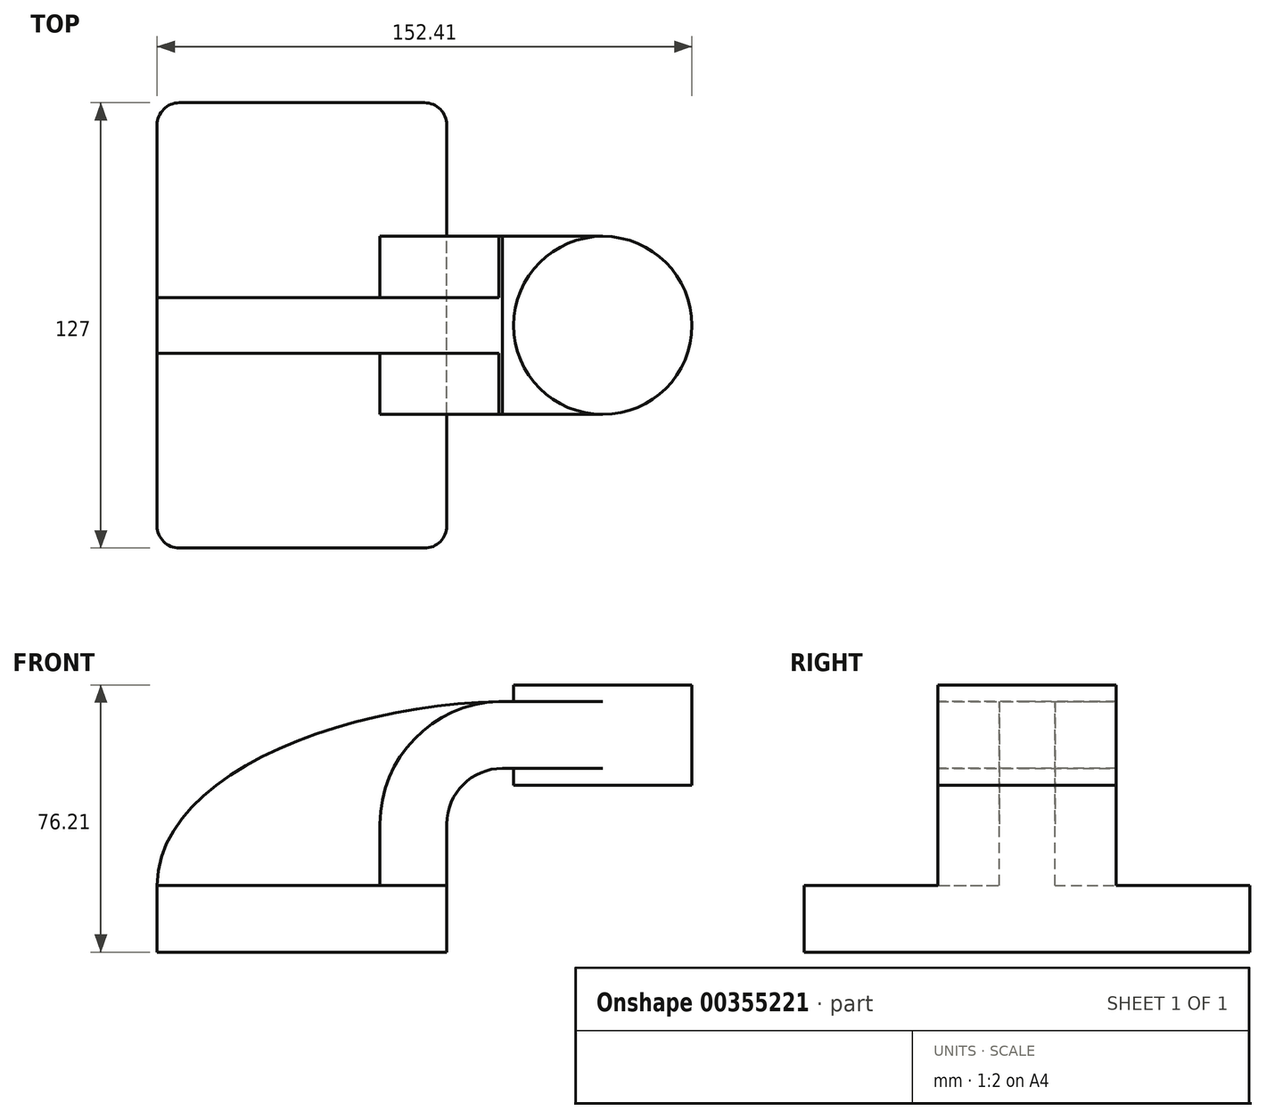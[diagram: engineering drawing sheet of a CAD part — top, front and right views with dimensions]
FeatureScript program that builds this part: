
annotation { "Feature Type Name" : "Feature", "Feature Type Description" : "" }
export const myFeature = defineFeature(function(context is Context, id is Id, definition is map)
    precondition{}
    {
        {
            var Q0;
            Q0=qCreatedBy(makeId("Front.planeOp"),FACE);
            var sketch = newSketch(context, id + "F0", { "sketchPlane" : qUnion([Q0])});
            skLineSegment(sketch, "E0.bottom", {"start": v(-41.28, 9.52) * mm, "end": v(41.28, 9.52) * mm});
            skLineSegment(sketch, "E0.top", {"start": v(-41.28, -9.53) * mm, "end": v(41.28, -9.53) * mm});
            skLineSegment(sketch, "E0.left", {"start": v(-41.28, 9.52) * mm, "end": v(-41.28, -9.53) * mm});
            skLineSegment(sketch, "E0.right", {"start": v(41.28, 9.53) * mm, "end": v(41.28, -9.53) * mm});
            skPoint(sketch, "E0.middle", {"position": v(0, 0) * mm});
            skLineSegment(sketch, "E1.bottom", {"start": v(111.12, 38.1) * mm, "end": v(60.32, 38.1) * mm});
            skLineSegment(sketch, "E1.top", {"start": v(111.12, 66.68) * mm, "end": v(60.32, 66.68) * mm});
            skLineSegment(sketch, "E1.left", {"start": v(111.12, 38.1) * mm, "end": v(111.12, 66.68) * mm});
            skLineSegment(sketch, "E1.right", {"start": v(60.32, 38.1) * mm, "end": v(60.32, 66.68) * mm});
            skPoint(sketch, "E1.middle", {"position": v(85.72, 52.39) * mm});
            skLineSegment(sketch, "E2", {"start": v(41.27, 9.53) * mm, "end": v(41.27, 27) * mm});
            skArc(sketch, "E3", {"start": v(41.27, 27) * mm, "mid": v(45.92, 38.23) * mm, "end": v(57.15, 42.88) * mm});
            skLineSegment(sketch, "E4", {"start": v(57.15, 42.88) * mm, "end": v(85.72, 42.88) * mm});
            skPoint(sketch, "E4.endSnap0", {"position": v(85.72, 66.68) * mm});
            skLineSegment(sketch, "E5.0", {"start": v(57.15, 61.93) * mm, "end": v(85.72, 61.93) * mm});
            skArc(sketch, "E5.1", {"start": v(22.23, 27) * mm, "mid": v(32.45, 51.7) * mm, "end": v(57.15, 61.93) * mm});
            skLineSegment(sketch, "E5.2", {"start": v(22.22, 9.53) * mm, "end": v(22.22, 27) * mm});
            skLineSegment(sketch, "E6", {"start": v(85.72, 38.1) * mm, "end": v(85.72, 66.68) * mm});
            skFitSpline(sketch, "E7", {"points": [v(-41.28, 9.52) * mm, v(57.15, 61.93) * mm], "startDerivative": vector(0.82, 96.4) * mm, "endDerivative": vector(132.46, 1.6) * mm});
            skSolve(sketch);
        }
        {
            var Q0;
            Q0=makeQuery(id+"F0.imprint","IMPRINT",FACE,{"disambiguationData":[TD([[makeQuery(id+"F0.imprint","IMPRINT",EDGE,{"derivedFrom":sQuery(id+"F0.wireOp",EDGE,"E0.top")}),1.0]])]});
            extrude(context, id + "F1", {"entities" : qUnion([Q0]), "endBound" : BoundingType.SYMMETRIC, "depth" : 127 * mm});
        }
        {
            var Q0;
            {var subQ1=sQuery(id+"F0.wireOp",EDGE,"E2");Q0=makeQuery(id+"F0.imprint","IMPRINT",FACE,{"disambiguationData":[TD([[makeQuery(id+"F0.imprint","IMPRINT",EDGE,{"derivedFrom":subQ1}),1.0]])]});}
            var Q1;
            {var subQ0=sQuery(id+"F0.wireOp",EDGE,"E4");var subQ1=sQuery(id+"F0.wireOp",EDGE,"E1.right");var subQ2=makeQuery(id+"F0.imprint","INTERSECT",VERTEX,{"derivedFrom":[subQ1,subQ0]});Q1=makeQuery(id+"F0.imprint","IMPRINT",FACE,{"disambiguationData":[TD([[makeQuery(id+"F0.imprint","IMPRINT",EDGE,{"disambiguationData":[TD([[subQ2,-1.0]])],"derivedFrom":subQ1}),-1.0]])]});}
            extrude(context, id + "F2", {"entities" : qUnion([Q0, Q1]), "operationType" : NewBodyOperationType.ADD, "endBound" : BoundingType.SYMMETRIC, "depth" : 50.8 * mm});
        }
        {
            var Q0;
            {var subQ3=sQuery(id+"F0.wireOp",EDGE,"E5.2");Q0=makeQuery(id+"F0.imprint","IMPRINT",FACE,{"disambiguationData":[TD([[makeQuery(id+"F0.imprint","IMPRINT",EDGE,{"derivedFrom":subQ3}),1.0]])]});}
            extrude(context, id + "F3", {"entities" : qUnion([Q0]), "operationType" : NewBodyOperationType.ADD, "endBound" : BoundingType.SYMMETRIC, "depth" : 15.88 * mm});
        }
        {
            var Q0;
            {var subQ0=sQuery(id+"F0.wireOp",EDGE,"E1.left");Q0=makeQuery(id+"F0.imprint","IMPRINT",FACE,{"disambiguationData":[TD([[makeQuery(id+"F0.imprint","IMPRINT",EDGE,{"derivedFrom":subQ0}),1.0]])]});}
            var Q1;
            Q1=sQuery(id+"F0.wireOp",EDGE,"E6");
            revolve(context, id + "F4", {"operationType" : NewBodyOperationType.ADD, "entities" : qUnion([Q0]), "axis" : qUnion([Q1]), "revolveType" : RevolveType.FULL});
        }
        {
            var Q0;
            Q0=makeQuery(id+"F1.opExtrude","CAP_EDGE",EDGE,{"disambiguationData":[OSD([sQuery(id+"F0.wireOp",EDGE,"E0.right")])],"isStart":false});
            var Q1;
            Q1=makeQuery(id+"F1.opExtrude","CAP_EDGE",EDGE,{"disambiguationData":[OSD([sQuery(id+"F0.wireOp",EDGE,"E0.left")])],"isStart":false});
            var Q2;
            Q2=makeQuery(id+"F1.opExtrude","CAP_EDGE",EDGE,{"disambiguationData":[OSD([sQuery(id+"F0.wireOp",EDGE,"E0.right")])],"isStart":true});
            var Q3;
            Q3=makeQuery(id+"F1.opExtrude","CAP_EDGE",EDGE,{"disambiguationData":[OSD([sQuery(id+"F0.wireOp",EDGE,"E0.left")])],"isStart":true});
            fillet(context, id + "F5", {"entities" : qUnion([Q0, Q1, Q2, Q3]), "radius" : 6.35 * mm, "tangentPropagation" : true, "allowEdgeOverflow" : false});
        }
    });
